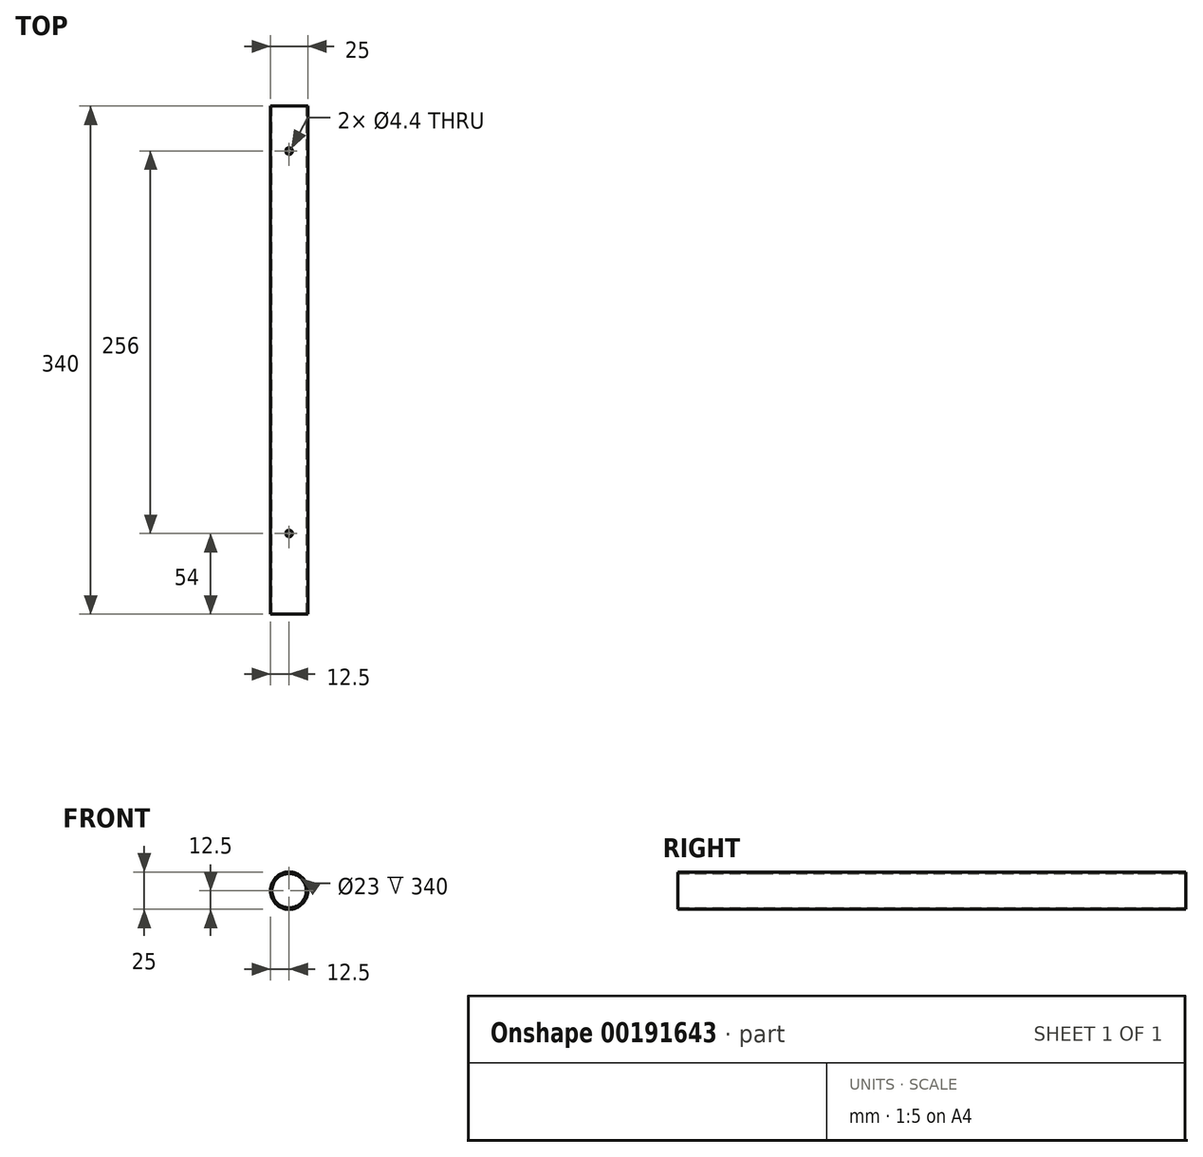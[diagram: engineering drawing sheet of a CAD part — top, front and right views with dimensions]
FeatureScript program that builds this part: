
annotation { "Feature Type Name" : "Feature", "Feature Type Description" : "" }
export const myFeature = defineFeature(function(context is Context, id is Id, definition is map)
    precondition{}
    {
        {
            var Q0;
            Q0=qCreatedBy(makeId("Front.planeOp"),FACE);
            var sketch = newSketch(context, id + "F0", { "sketchPlane" : qUnion([Q0])});
            skCircle(sketch, "E0", {"center": v(0, 0) * mm, "radius": 12.5 * mm});
            skCircle(sketch, "E1", {"center": v(0, 0) * mm, "radius": 11.5 * mm});
            skSolve(sketch);
        }
        {
            var Q0;
            Q0 = qSketchRegion(id + "F0", true);
            extrude(context, id + "F1", {"entities" : qUnion([Q0]), "depth" : 340 * mm});
        }
        {
            var Q0;
            Q0=qCreatedBy(makeId("Top.planeOp"),FACE);
            var sketch = newSketch(context, id + "F2", { "sketchPlane" : qUnion([Q0])});
            skPoint(sketch, "E2", {"position": v(0, -30) * mm});
            skPoint(sketch, "E3", {"position": v(0, -286) * mm});
            skSolve(sketch);
        }
        {
            var Q0;
            Q0=sQuery(id+"F2.wireOp",VERTEX,"E2");
            var Q1;
            Q1=sQuery(id+"F2.wireOp",VERTEX,"f824ff2b-5403-4162-87b4-e8ee4a379916");
            var Q2;
            Q2=sQuery(id+"F2.wireOp",VERTEX,"E3");
            var Q3;
            Q3=makeQuery(id+"F1.opExtrude","SWEPT_BODY",BODY,{"disambiguationData":[OSD([sQuery(id+"F0.wireOp",EDGE,"E0"),sQuery(id+"F0.wireOp",EDGE,"E1")])]});
            hole(context, id + "F3", {"style" : HoleStyle.SIMPLE, "endStyle" : HoleEndStyle.THROUGH, "oppositeDirection" : true, "standardTappedOrClearance" : lookupTablePath({ "standard" : "ISO", "fit" : "Normal", "size" : "M4", "type" : "Clearance" }), "standardBlindInLast" : lookupTablePath({ "fit" : "Standard", "standard" : "ISO", "size" : "M4", "type" : "Clearance" }), "holeDiameter" : 4.4 * mm, "locations" : qUnion([Q0, Q1, Q2]), "scope" : qUnion([Q3]), "isTappedThrough" : true});
        }
    });
